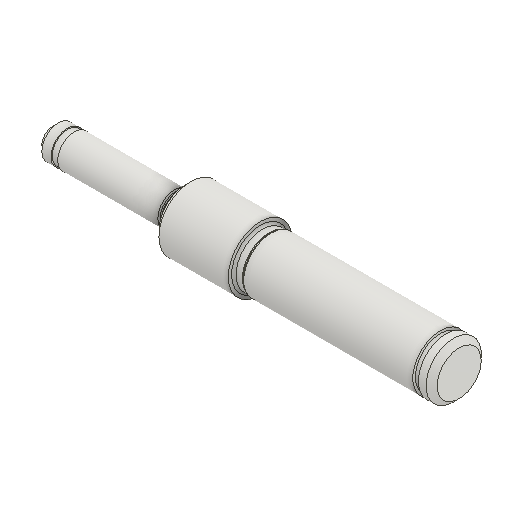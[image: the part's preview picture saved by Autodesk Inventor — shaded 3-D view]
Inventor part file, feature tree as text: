
AUTODESK INVENTOR PART (.ipt)
format: ipt  version: 2025.1 (Build 291241000, 241)  size: 178,176 bytes
history: native  units: mm
features: other x13, chamfer x3, revolve x1
ambient origin geometry x6: Origin, XZ Plane, XY Plane, X Axis, Y Axis, Z Axis
bodies: Body1 (feature_tree)
feature tree (17):
  other  "{BB8FE430-83BF-418D-8DF9-9B323D3DB9B9}"
  other  "Bryła1"
  revolve  "Obrót1"
  other  "Rowek dla pierścienia zabezpieczającego2"
  chamfer  "Faza4"  [1 undecoded]
  chamfer  "Faza1"  Distance=3.0mm
  other  "Podcięcie1"
  other  "Podcięcie2"
  chamfer  "Faza3"  Distance=5.8mm
  other  "Rowek dla pierścienia zabezpieczającego1"
  other  "Płaszczyzna początkowa"
  other  "Punkt początkowy"
  other  "Szkic główny"
  other  "iFeature2:1"
  other  "iFeature2:2"
  other  "iFeature27:1"
  other  "iFeature27:2"
note: 1 required parameter value undecoded (feature->parameter linkage not recoverable at this tier; creation-order binding heuristic only, values carry confidence <= 0.55)
